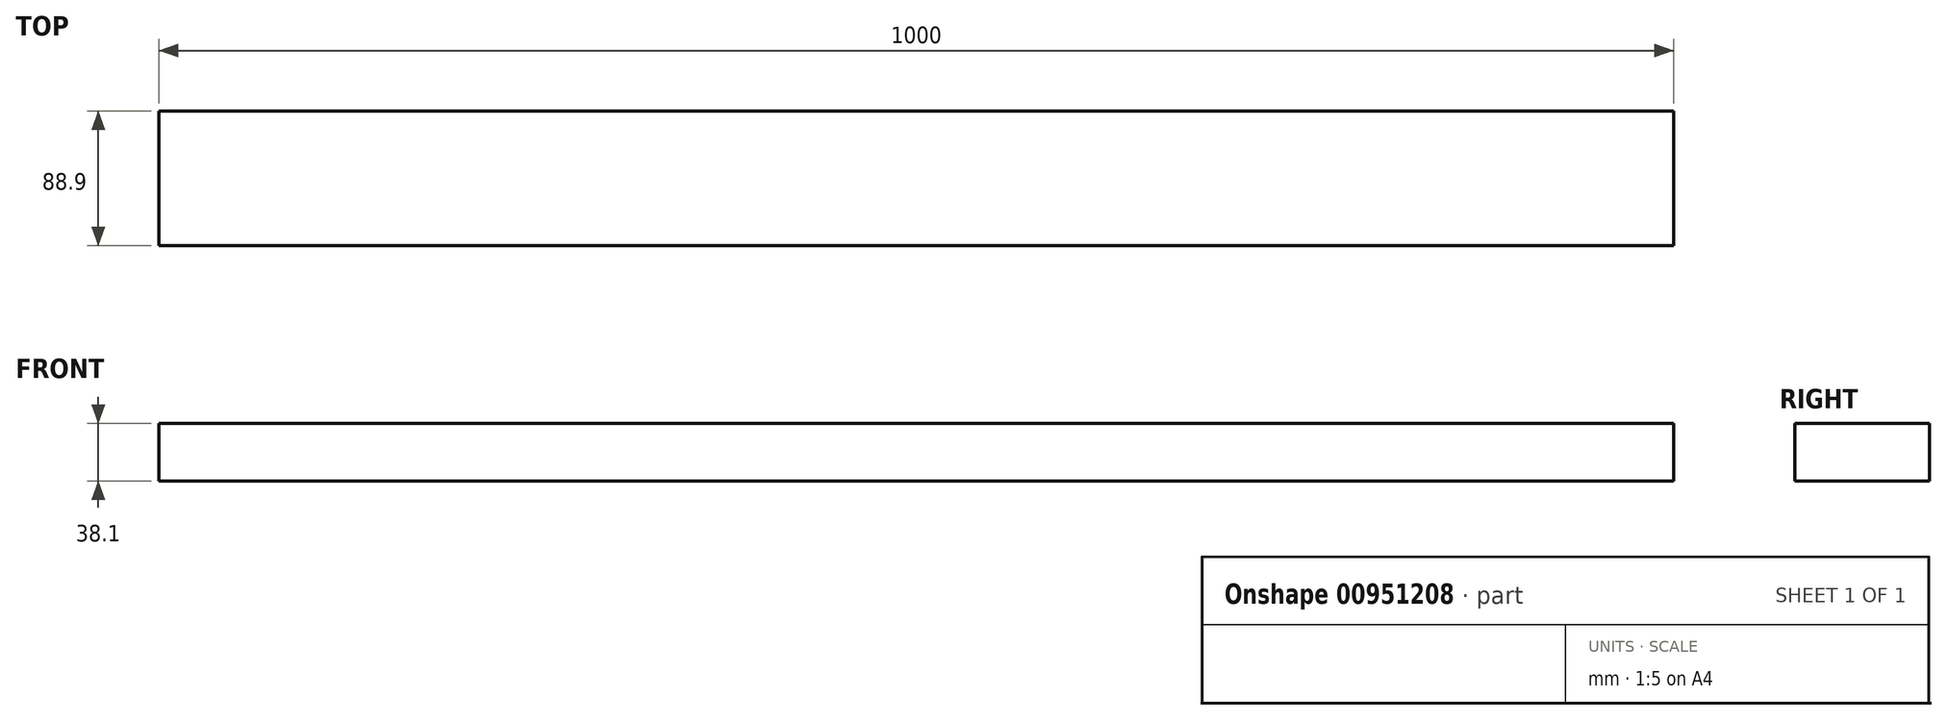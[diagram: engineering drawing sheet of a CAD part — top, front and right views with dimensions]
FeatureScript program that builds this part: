
annotation { "Feature Type Name" : "Feature", "Feature Type Description" : "" }
export const myFeature = defineFeature(function(context is Context, id is Id, definition is map)
    precondition{}
    {
        {
            var Q0;
            Q0=qCreatedBy(makeId("Right.planeOp"),FACE);
            var sketch = newSketch(context, id + "F0", { "sketchPlane" : qUnion([Q0])});
            skLineSegment(sketch, "E0.bottom", {"start": v(44.45, -19.05) * mm, "end": v(-44.45, -19.05) * mm});
            skLineSegment(sketch, "E0.top", {"start": v(44.45, 19.05) * mm, "end": v(-44.45, 19.05) * mm});
            skLineSegment(sketch, "E0.left", {"start": v(44.45, -19.05) * mm, "end": v(44.45, 19.05) * mm});
            skLineSegment(sketch, "E0.right", {"start": v(-44.45, -19.05) * mm, "end": v(-44.45, 19.05) * mm});
            skPoint(sketch, "E0.middle", {"position": v(0, 0) * mm});
            skSolve(sketch);
        }
        {
            var Q0;
            Q0=qSketchRegion(id+"F0",true);
            var Q1;
            Q1=makeQuery(id+"F0.imprint","IMPRINT",FACE,{"disambiguationData":[TD([[makeQuery(id+"F0.imprint","IMPRINT",EDGE,{"derivedFrom":sQuery(id+"F0.wireOp",EDGE,"E0.bottom")}),-1.0]])]});
            extrude(context, id + "F1", {"entities" : qUnion([Q0, Q1]), "depth" : 1000 * mm, "offsetDistance" : 25.4 * mm});
        }
    });
